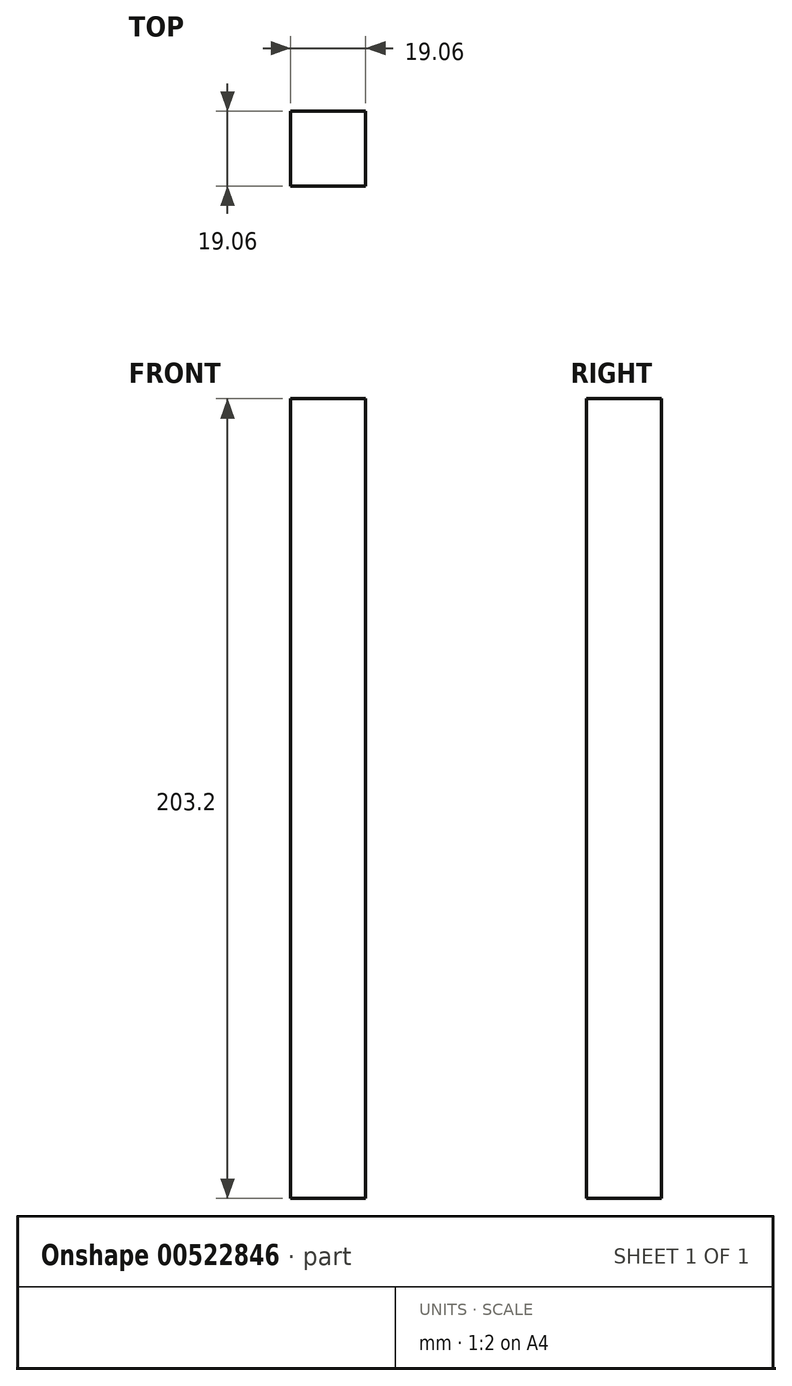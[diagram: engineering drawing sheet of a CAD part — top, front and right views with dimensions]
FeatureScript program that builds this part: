
annotation { "Feature Type Name" : "Feature", "Feature Type Description" : "" }
export const myFeature = defineFeature(function(context is Context, id is Id, definition is map)
    precondition{}
    {
        {
            var Q0;
            Q0=qCreatedBy(makeId("Top.planeOp"),FACE);
            var sketch = newSketch(context, id + "F0", { "sketchPlane" : qUnion([Q0])});
            skLineSegment(sketch, "E0.bottom", {"start": v(-9.52, 9.53) * mm, "end": v(9.53, 9.53) * mm});
            skLineSegment(sketch, "E0.top", {"start": v(-9.53, -9.52) * mm, "end": v(9.53, -9.52) * mm});
            skLineSegment(sketch, "E0.left", {"start": v(-9.52, 9.53) * mm, "end": v(-9.53, -9.52) * mm});
            skLineSegment(sketch, "E0.right", {"start": v(9.53, 9.53) * mm, "end": v(9.53, -9.52) * mm});
            skPoint(sketch, "E0.middle", {"position": v(0, 0) * mm});
            skSolve(sketch);
        }
        {
            var Q0;
            Q0=makeQuery(id+"F0.imprint","IMPRINT",FACE,{"disambiguationData":[TD([[makeQuery(id+"F0.imprint","IMPRINT",EDGE,{"derivedFrom":sQuery(id+"F0.wireOp",EDGE,"E0.bottom")}),-1.0]])]});
            extrude(context, id + "F1", {"entities" : qUnion([Q0]), "depth" : 203.2 * mm, "offsetDistance" : 25.4 * mm});
        }
    });
